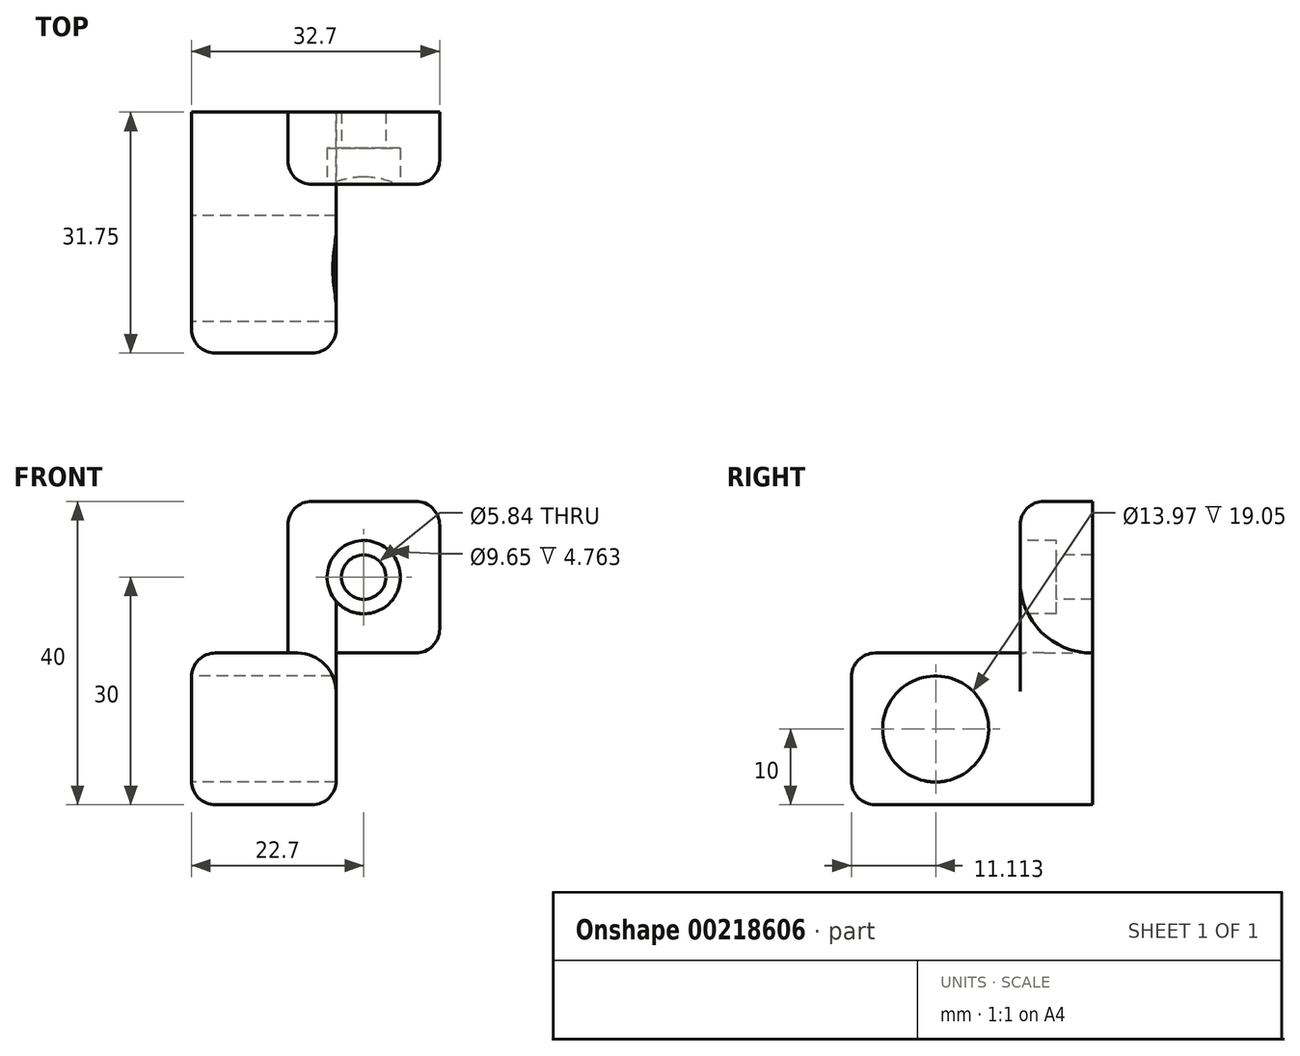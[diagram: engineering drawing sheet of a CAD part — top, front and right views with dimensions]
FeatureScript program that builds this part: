
annotation { "Feature Type Name" : "Feature", "Feature Type Description" : "" }
export const myFeature = defineFeature(function(context is Context, id is Id, definition is map)
    precondition{}
    {
        {
            var Q0;
            Q0=qCreatedBy(makeId("Front.planeOp"),FACE);
            var sketch = newSketch(context, id + "F0", { "sketchPlane" : qUnion([Q0])});
            skLineSegment(sketch, "E0.bottom", {"start": v(10, -10) * mm, "end": v(-10, -10) * mm});
            skLineSegment(sketch, "E0.top", {"start": v(10, 10) * mm, "end": v(-10, 10) * mm});
            skLineSegment(sketch, "E0.left", {"start": v(10, -10) * mm, "end": v(10, 10) * mm});
            skLineSegment(sketch, "E0.right", {"start": v(-10, -10) * mm, "end": v(-10, 10) * mm});
            skPoint(sketch, "E0.middle", {"position": v(0, 0) * mm});
            skSolve(sketch);
        }
        {
            var Q0;
            Q0=makeQuery(id+"F0.imprint","IMPRINT",FACE,{"disambiguationData":[TD([[makeQuery(id+"F0.imprint","IMPRINT",EDGE,{"derivedFrom":sQuery(id+"F0.wireOp",EDGE,"E0.bottom")}),-1.0]])]});
            extrude(context, id + "F1", {"entities" : qUnion([Q0]), "depth" : 9.52 * mm, "offsetDistance" : 25.4 * mm});
        }
        {
            var Q0;
            Q0=makeQuery(id+"F1.opExtrude","SWEPT_FACE",FACE,{"disambiguationData":[OSD([sQuery(id+"F0.wireOp",EDGE,"E0.right")])]});
            var sketch = newSketch(context, id + "F2", { "sketchPlane" : qUnion([Q0])});
            skLineSegment(sketch, "E1", {"start": v(0, -10) * mm, "end": v(0, -30) * mm});
            skLineSegment(sketch, "E2", {"start": v(31.75, -30) * mm, "end": v(0, -30) * mm});
            skLineSegment(sketch, "E3", {"start": v(31.75, -30) * mm, "end": v(31.75, -10) * mm});
            skLineSegment(sketch, "E4", {"start": v(0, -10) * mm, "end": v(31.75, -10) * mm});
            skSolve(sketch);
        }
        {
            var Q0;
            Q0 = qSketchRegion(id + "F2", true);
            var Q1;
            Q1=makeQuery(id+"F1.opExtrude","SWEPT_FACE",FACE,{"disambiguationData":[OSD([sQuery(id+"F0.wireOp",EDGE,"E0.right")])]});
            extrude(context, id + "F3", {"entities" : qUnion([Q0]), "operationType" : NewBodyOperationType.ADD, "oppositeDirection" : true, "depth" : 6.35 * mm, "endBoundEntityFace" : qUnion([Q1]), "offsetDistance" : 25.4 * mm, "hasSecondDirection" : true, "secondDirectionOppositeDirection" : false, "secondDirectionDepth" : 12.7 * mm});
        }
        {
            var Q0;
            {var subQ0=sQuery(id+"F0.wireOp",EDGE,"E0.bottom");Q0=makeQuery(id+"F3.boolean.opBoolean","SPLIT",EDGE,{"disambiguationData":[topologyDisambiguationEdgeConnected([makeQuery(id+"F3.opExtrude","SWEPT_FACE",FACE,{"disambiguationData":[OSD([sQuery(id+"F2.wireOp",EDGE,"E4")])]})])],"derivedFrom":makeQuery(id+"F1.opExtrude","CAP_EDGE",EDGE,{"disambiguationData":[OSD([subQ0])],"isStart":false})});}
            var Q1;
            Q1=makeQuery(id+"F1.opExtrude","SWEPT_EDGE",EDGE,{"disambiguationData":[OSD([sQuery(id+"F0.wireOp",EDGE,"E0.bottom"),sQuery(id+"F0.wireOp",EDGE,"E0.right")])]});
            fillet(context, id + "F4", {"entities" : qUnion([Q0, Q1]), "tangentPropagation" : true, "radius" : 9.52 * mm, "defaultsChanged" : true, "vertexSettings" : [], "allowEdgeOverflow" : false});
        }
        {
            var Q0;
            {var subQ0=sQuery(id+"F2.wireOp",EDGE,"E4");var subQ1=sQuery(id+"F0.wireOp",EDGE,"E0.bottom");Q0=makeQuery(id+"F4.opFillet","TWEAK_EDGE",EDGE,{"derivedFrom":[makeQuery(id+"F3.boolean.opBoolean","TWEAK_VERTEX",VERTEX,{"derivedFrom":[makeQuery(id+"F1.opExtrude","SWEPT_FACE",FACE,{"disambiguationData":[OSD([subQ1])]}),makeQuery(id+"F1.opExtrude","CAP_FACE",FACE,{"disambiguationData":[OSD([subQ1,sQuery(id+"F0.wireOp",EDGE,"E0.top"),sQuery(id+"F0.wireOp",EDGE,"E0.left"),sQuery(id+"F0.wireOp",EDGE,"E0.right")])],"isStart":false}),makeQuery(id+"F3.opExtrude","CAP_FACE",FACE,{"disambiguationData":[OSD([sQuery(id+"F2.wireOp",EDGE,"E1"),sQuery(id+"F2.wireOp",EDGE,"E2"),sQuery(id+"F2.wireOp",EDGE,"E3"),subQ0])],"isStart":false}),makeQuery(id+"F3.opExtrude","SWEPT_FACE",FACE,{"disambiguationData":[OSD([subQ0])]})]})]});}
            var Q1;
            {var subQ0=sQuery(id+"F2.wireOp",EDGE,"E4");Q1=makeQuery(id+"F3.boolean.opBoolean","SPLIT",EDGE,{"disambiguationData":[topologyDisambiguationEdgeConnected([makeQuery(id+"F1.opExtrude","SWEPT_FACE",FACE,{"disambiguationData":[OSD([sQuery(id+"F0.wireOp",EDGE,"E0.bottom")])]})])],"derivedFrom":makeQuery(id+"F3.opExtrude","CAP_EDGE",EDGE,{"disambiguationData":[OSD([subQ0])],"isStart":false})});}
            fillet(context, id + "F5", {"entities" : qUnion([Q0, Q1]), "tangentPropagation" : true, "radius" : 5.08 * mm, "defaultsChanged" : false, "vertexSettings" : [], "allowEdgeOverflow" : false});
        }
        {
            var Q0;
            Q0=makeQuery(id+"F1.opExtrude","CAP_FACE",FACE,{"disambiguationData":[OSD([sQuery(id+"F0.wireOp",EDGE,"E0.bottom"),sQuery(id+"F0.wireOp",EDGE,"E0.top"),sQuery(id+"F0.wireOp",EDGE,"E0.left"),sQuery(id+"F0.wireOp",EDGE,"E0.right")])],"isStart":false});
            var sketch = newSketch(context, id + "F6", { "sketchPlane" : qUnion([Q0])});
            skCircle(sketch, "E5", {"center": v(0, 0) * mm, "radius": 2.92 * mm});
            skSolve(sketch);
        }
        {
            var Q0;
            Q0 = qSketchRegion(id + "F6", true);
            extrude(context, id + "F7", {"entities" : qUnion([Q0]), "operationType" : NewBodyOperationType.REMOVE, "endBound" : BoundingType.THROUGH_ALL, "oppositeDirection" : true, "depth" : 25.4 * mm, "offsetDistance" : 25.4 * mm, "hasSecondDirection" : true, "secondDirectionBound" : BoundingType.THROUGH_ALL, "secondDirectionOppositeDirection" : false, "secondDirectionDepth" : 25.4 * mm});
        }
        {
            var Q0;
            Q0=makeQuery(id+"F1.opExtrude","CAP_FACE",FACE,{"disambiguationData":[OSD([sQuery(id+"F0.wireOp",EDGE,"E0.bottom"),sQuery(id+"F0.wireOp",EDGE,"E0.top"),sQuery(id+"F0.wireOp",EDGE,"E0.left"),sQuery(id+"F0.wireOp",EDGE,"E0.right")])],"isStart":false});
            var sketch = newSketch(context, id + "F8", { "sketchPlane" : qUnion([Q0])});
            skCircle(sketch, "E6", {"center": v(0, 0) * mm, "radius": 4.83 * mm});
            skSolve(sketch);
        }
        {
            var Q0;
            Q0 = qSketchRegion(id + "F8", true);
            extrude(context, id + "F9", {"entities" : qUnion([Q0]), "operationType" : NewBodyOperationType.REMOVE, "oppositeDirection" : true, "depth" : 4.76 * mm, "offsetDistance" : 25.4 * mm, "hasSecondDirection" : true, "secondDirectionBound" : BoundingType.THROUGH_ALL, "secondDirectionOppositeDirection" : false, "secondDirectionDepth" : 25.4 * mm});
        }
        {
            var Q0;
            Q0=makeQuery(id+"F3.opExtrude","CAP_FACE",FACE,{"disambiguationData":[OSD([sQuery(id+"F2.wireOp",EDGE,"E1"),sQuery(id+"F2.wireOp",EDGE,"E2"),sQuery(id+"F2.wireOp",EDGE,"E3"),sQuery(id+"F2.wireOp",EDGE,"E4")])],"isStart":true});
            var sketch = newSketch(context, id + "F10", { "sketchPlane" : qUnion([Q0])});
            skCircle(sketch, "E7", {"center": v(20.64, -20) * mm, "radius": 6.99 * mm});
            skLineSegment(sketch, "E8", {"start": v(31.75, -30) * mm, "end": v(9.53, -30) * mm, "construction": true});
            skPoint(sketch, "E9", {"position": v(20.64, -30) * mm});
            skSolve(sketch);
        }
        {
            var Q0;
            Q0 = qSketchRegion(id + "F10", true);
            extrude(context, id + "F11", {"entities" : qUnion([Q0]), "operationType" : NewBodyOperationType.REMOVE, "endBound" : BoundingType.THROUGH_ALL, "oppositeDirection" : true, "depth" : 25.4 * mm, "offsetDistance" : 25.4 * mm});
        }
        {
            var Q0;
            Q0=makeQuery(id+"F3.opExtrude","CAP_EDGE",EDGE,{"disambiguationData":[OSD([sQuery(id+"F2.wireOp",EDGE,"E4")])],"isStart":true});
            var Q1;
            Q1=makeQuery(id+"F3.opExtrude","SWEPT_EDGE",EDGE,{"disambiguationData":[OSD([sQuery(id+"F2.wireOp",EDGE,"E3"),sQuery(id+"F2.wireOp",EDGE,"E4")])]});
            var Q2;
            Q2=makeQuery(id+"F3.opExtrude","CAP_EDGE",EDGE,{"disambiguationData":[OSD([sQuery(id+"F2.wireOp",EDGE,"E2")])],"isStart":true});
            var Q3;
            Q3=makeQuery(id+"F3.opExtrude","CAP_EDGE",EDGE,{"disambiguationData":[OSD([sQuery(id+"F2.wireOp",EDGE,"E3")])],"isStart":true});
            var Q4;
            Q4=makeQuery(id+"F3.opExtrude","SWEPT_EDGE",EDGE,{"disambiguationData":[OSD([sQuery(id+"F2.wireOp",EDGE,"E2"),sQuery(id+"F2.wireOp",EDGE,"E3")])]});
            var Q5;
            Q5=makeQuery(id+"F3.opExtrude","CAP_EDGE",EDGE,{"disambiguationData":[OSD([sQuery(id+"F2.wireOp",EDGE,"E3")])],"isStart":false});
            var Q6;
            Q6=makeQuery(id+"F3.opExtrude","CAP_EDGE",EDGE,{"disambiguationData":[OSD([sQuery(id+"F2.wireOp",EDGE,"E2")])],"isStart":false});
            var Q7;
            Q7=makeQuery(id+"F1.opExtrude","CAP_EDGE",EDGE,{"disambiguationData":[OSD([sQuery(id+"F0.wireOp",EDGE,"E0.left")])],"isStart":false});
            var Q8;
            {var subQ0=sQuery(id+"F0.wireOp",EDGE,"E0.bottom");Q8=makeQuery(id+"F3.boolean.opBoolean","SPLIT",EDGE,{"disambiguationData":[topologyDisambiguationEdgeConnected([makeQuery(id+"F1.opExtrude","SWEPT_FACE",FACE,{"disambiguationData":[OSD([subQ0])]})])],"derivedFrom":makeQuery(id+"F1.opExtrude","CAP_EDGE",EDGE,{"disambiguationData":[OSD([subQ0])],"isStart":false})});}
            var Q9;
            Q9=makeQuery(id+"F1.opExtrude","SWEPT_EDGE",EDGE,{"disambiguationData":[OSD([sQuery(id+"F0.wireOp",EDGE,"E0.bottom"),sQuery(id+"F0.wireOp",EDGE,"E0.left")])]});
            var Q10;
            Q10=makeQuery(id+"F1.opExtrude","SWEPT_EDGE",EDGE,{"disambiguationData":[OSD([sQuery(id+"F0.wireOp",EDGE,"E0.top"),sQuery(id+"F0.wireOp",EDGE,"E0.left")])]});
            var Q11;
            Q11=makeQuery(id+"F1.opExtrude","CAP_EDGE",EDGE,{"disambiguationData":[OSD([sQuery(id+"F0.wireOp",EDGE,"E0.top")])],"isStart":false});
            var Q12;
            Q12=makeQuery(id+"F1.opExtrude","SWEPT_EDGE",EDGE,{"disambiguationData":[OSD([sQuery(id+"F0.wireOp",EDGE,"E0.top"),sQuery(id+"F0.wireOp",EDGE,"E0.right")])]});
            var Q13;
            Q13=makeQuery(id+"F1.opExtrude","CAP_EDGE",EDGE,{"disambiguationData":[OSD([sQuery(id+"F0.wireOp",EDGE,"E0.right")])],"isStart":false});
            var Q14;
            {var subQ0=sQuery(id+"F2.wireOp",EDGE,"E4");Q14=makeQuery(id+"F3.boolean.opBoolean","SPLIT",EDGE,{"disambiguationData":[topologyDisambiguationEdgeConnected([makeQuery(id+"F3.opExtrude","SWEPT_FACE",FACE,{"disambiguationData":[OSD([subQ0])]})])],"derivedFrom":makeQuery(id+"F3.opExtrude","CAP_EDGE",EDGE,{"disambiguationData":[OSD([subQ0])],"isStart":false})});}
            fillet(context, id + "F12", {"entities" : qUnion([Q0, Q1, Q2, Q3, Q4, Q5, Q6, Q7, Q8, Q9, Q10, Q11, Q12, Q13, Q14]), "tangentPropagation" : true, "radius" : 3.17 * mm, "defaultsChanged" : false, "vertexSettings" : [], "allowEdgeOverflow" : false});
        }
    });
